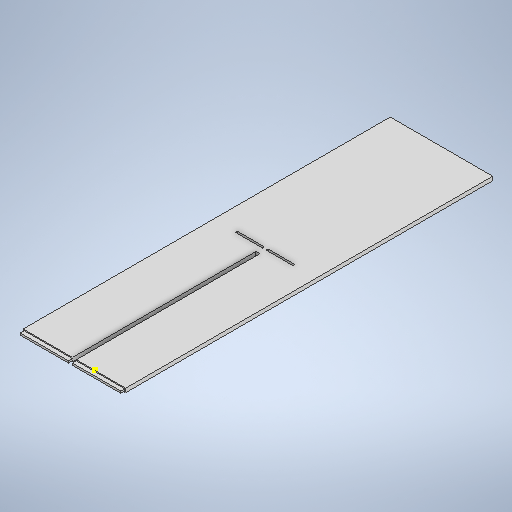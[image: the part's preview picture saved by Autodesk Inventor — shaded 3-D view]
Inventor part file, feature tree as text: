
AUTODESK INVENTOR PART (.ipt)
format: ipt  version: 2025.2 (Build 292293000, 293)  size: 379,904 bytes
history: native  units: mm
features: sketch x13, extrude x12, projected_geometry x3
ambient origin geometry x8: Origin, YZ Plane, XZ Plane, XY Plane, X Axis, Y Axis, Z Axis, Center Point
bodies: Solid1 (feature_tree)
feature tree (28):
  extrude  "Extrusion1"  Depth=447.675mm
  extrude  "Extrusion2"  Depth=4.7625mm TaperAngle=0.0deg
  extrude  "Extrusion3"  Depth=10.0mm TaperAngle=0.0deg
  extrude  "Extrusion4"  Depth=158.838mm TaperAngle=0.0deg
  sketch  "Sketch5"  dims[d25=4.763mm d26=223.837mm d27=0.0mm]
  extrude  "Extrusion5"  Depth=223.837mm TaperAngle=0.0deg
  extrude  "Extrusion6"  Depth=15.0mm TaperAngle=0.0deg
  extrude  "Extrusion7"  Depth=2.374mm TaperAngle=0.0deg
  extrude  "Extrusion8"  Depth=37.5mm
  extrude  "Extrusion9"  Depth=10.0mm TaperAngle=0.0deg
  extrude  "Extrusion10"  Depth=32.503mm TaperAngle=0.0deg
  extrude  "Extrusion11"  [1 undecoded]
  extrude  "Extrusion12"  [1 undecoded]
  sketch  "Sketch1"  dims[d0=50.0mm d1=447.675mm]
  sketch  "Sketch2"  dims[d2=4.7625mm d3=0.0mm d9=4.7625mm d10=0.0mm]
  sketch  "Sketch3"  dims[d11=25.0mm d18=10.0mm d19=0.0mm]
  sketch  "Sketch4"  dims[d20=10.0mm d21=0.0mm d22=158.838mm d23=0.0mm]
  sketch  "Sketch6"  dims[d28=15.0mm d29=0.0mm d30=15.0mm d31=0.0mm]
  projected_geometry  "Projected Loop1"
  sketch  "Sketch8"  dims[d35=2.374mm d36=10.0mm d37=0.0mm]
  sketch  "Sketch9"  dims[d39=37.5mm d40=37.5mm]
  projected_geometry  "Projected Loop2"
  sketch  "Sketch10"  dims[d41=10.0mm d42=0.0mm d44=10.0mm d45=0.0mm]
  projected_geometry  "Projected Loop3"
  sketch  "Sketch14"  dims[d47=32.503mm d48=10.0mm d49=0.0mm]
  sketch  "Sketch17"
  sketch  "Sketch18"
  sketch  "Sketch19"
note: 2 required parameter values undecoded (feature->parameter linkage not recoverable at this tier; creation-order binding heuristic only, values carry confidence <= 0.55)
